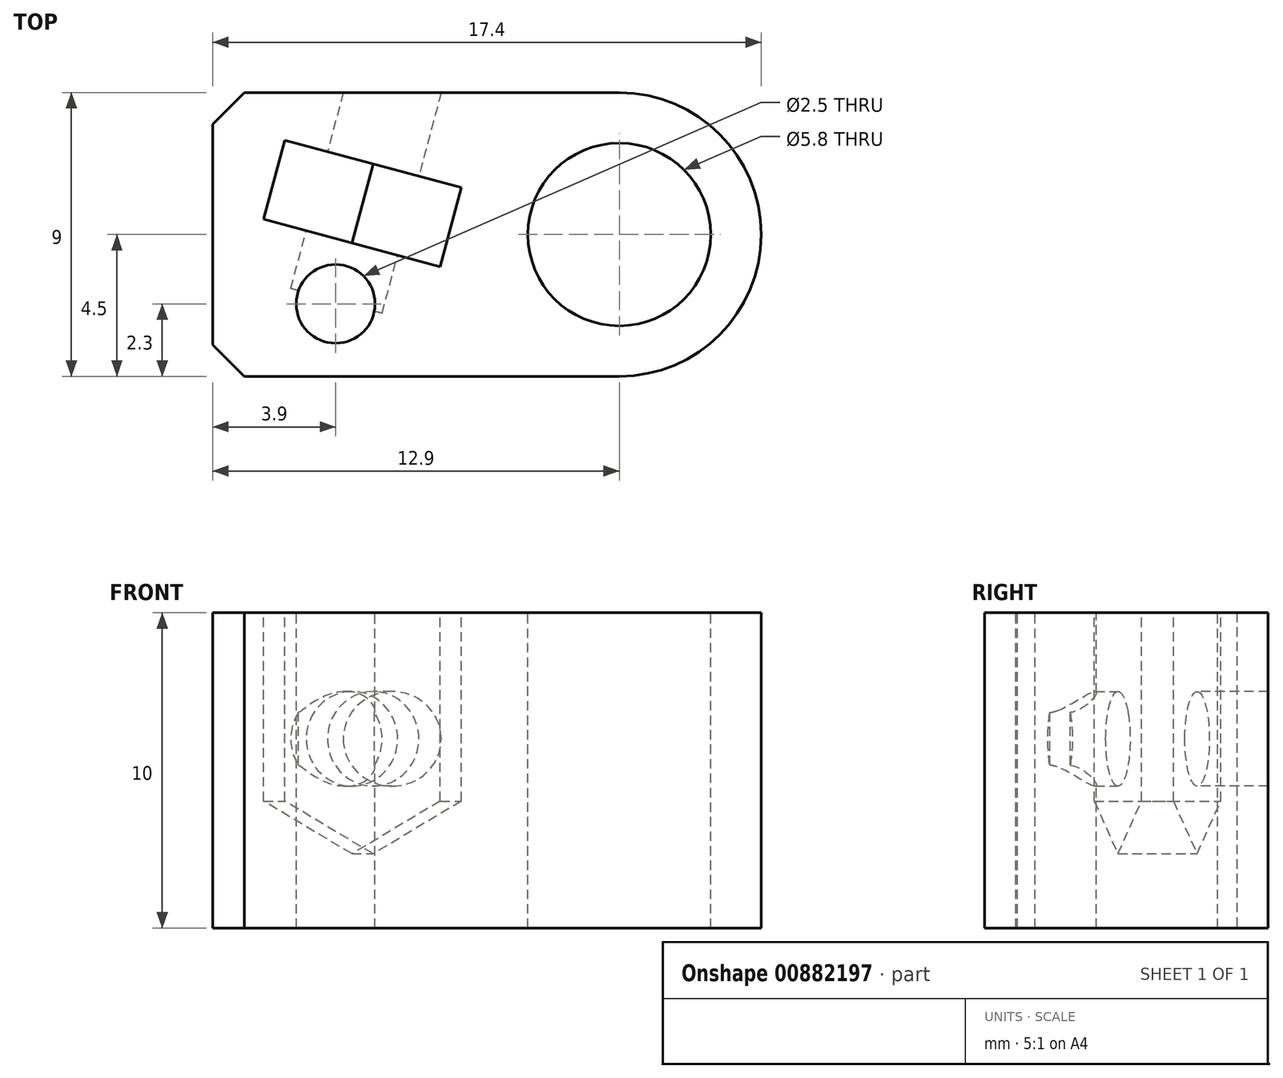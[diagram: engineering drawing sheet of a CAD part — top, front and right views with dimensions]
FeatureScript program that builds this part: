
annotation { "Feature Type Name" : "Feature", "Feature Type Description" : "" }
export const myFeature = defineFeature(function(context is Context, id is Id, definition is map)
    precondition{}
    {
        {
            var Q0;
            Q0=qCreatedBy(makeId("Top.planeOp"),FACE);
            var sketch = newSketch(context, id + "F0", { "sketchPlane" : qUnion([Q0])});
            skLineSegment(sketch, "E0.bottom", {"start": v(0, 0) * mm, "end": v(12.9, 0) * mm});
            skLineSegment(sketch, "E0.top", {"start": v(0, 9) * mm, "end": v(12.9, 9) * mm});
            skLineSegment(sketch, "E0.left", {"start": v(0, 0) * mm, "end": v(0, 9) * mm});
            skLineSegment(sketch, "E0.right", {"start": v(12.9, 0) * mm, "end": v(12.9, 9) * mm});
            skCircle(sketch, "E1", {"center": v(12.9, 4.5) * mm, "radius": 4.5 * mm});
            skCircle(sketch, "E2", {"center": v(12.9, 4.5) * mm, "radius": 2.9 * mm});
            skCircle(sketch, "E3", {"center": v(3.9, 2.3) * mm, "radius": 1.25 * mm});
            skSolve(sketch);
        }
        {
            var Q0;
            Q0=qSketchRegion(id+"F0",true);
            extrude(context, id + "F1", {"entities" : qUnion([Q0]), "oppositeDirection" : true, "depth" : 10 * mm, "offsetDistance" : 25 * mm});
        }
        {
            var Q0;
            Q0=makeQuery(id+"F1.opExtrude","CAP_FACE",FACE,{"disambiguationData":[OSD([sQuery(id+"F0.wireOp",EDGE,"E0.bottom"),sQuery(id+"F0.wireOp",EDGE,"E0.top"),sQuery(id+"F0.wireOp",EDGE,"E0.left"),sQuery(id+"F0.wireOp",EDGE,"E1"),sQuery(id+"F0.wireOp",EDGE,"E2"),sQuery(id+"F0.wireOp",EDGE,"E3")])],"isStart":true});
            var sketch = newSketch(context, id + "F2", { "sketchPlane" : qUnion([Q0])});
            skLineSegment(sketch, "E4.bottom", {"start": v(2.29, 7.5) * mm, "end": v(7.9, 6) * mm});
            skLineSegment(sketch, "E4.top", {"start": v(1.62, 4.98) * mm, "end": v(7.22, 3.48) * mm});
            skLineSegment(sketch, "E4.left", {"start": v(2.29, 7.5) * mm, "end": v(1.62, 4.98) * mm});
            skLineSegment(sketch, "E4.right", {"start": v(7.9, 6) * mm, "end": v(7.22, 3.48) * mm});
            skPoint(sketch, "E5", {"position": v(3.9, 2.3) * mm});
            skLineSegment(sketch, "E6", {"start": v(1.18, 2.3) * mm, "end": v(6.9, 2.3) * mm, "construction": true});
            skLineSegment(sketch, "E7", {"start": v(3.9, 2.3) * mm, "end": v(4.42, 4.23) * mm, "construction": true});
            skSolve(sketch);
        }
        {
            var Q0;
            Q0=makeQuery(id+"F2.imprint","IMPRINT",FACE,{"disambiguationData":[TD([[makeQuery(id+"F2.imprint","IMPRINT",EDGE,{"derivedFrom":sQuery(id+"F2.wireOp",EDGE,"E4.bottom")}),-1.0]])]});
            extrude(context, id + "F3", {"entities" : qUnion([Q0]), "operationType" : NewBodyOperationType.REMOVE, "oppositeDirection" : true, "depth" : 5 * mm, "offsetDistance" : 25 * mm});
        }
        {
            var Q0;
            Q0=makeQuery(id+"F3.boolean.opBoolean","COPY",FACE,{"derivedFrom":makeQuery(id+"F3.opExtrude","SWEPT_FACE",FACE,{"disambiguationData":[OSD([sQuery(id+"F2.wireOp",EDGE,"E4.bottom")])]})});
            var sketch = newSketch(context, id + "F4", { "sketchPlane" : qUnion([Q0])});
            skLineSegment(sketch, "E8.bottom", {"start": v(0.27, 0) * mm, "end": v(6.07, 0) * mm, "construction": true});
            skLineSegment(sketch, "E8.left", {"start": v(0.27, 0) * mm, "end": v(0.27, -5) * mm, "construction": true});
            skLineSegment(sketch, "E8.right", {"start": v(6.07, 0) * mm, "end": v(6.07, -5) * mm, "construction": true});
            skCircle(sketch, "E9.cCircle", {"center": v(3.17, -4.3) * mm, "radius": 2.9 * mm, "construction": true});
            skPoint(sketch, "E9.cCircle.centerSnap0", {"position": v(3.17, -5) * mm});
            skLineSegment(sketch, "E9.0", {"start": v(6.07, -2.63) * mm, "end": v(6.07, -5.97) * mm});
            skLineSegment(sketch, "E9.1", {"start": v(6.07, -5.97) * mm, "end": v(3.17, -7.65) * mm});
            skLineSegment(sketch, "E9.2", {"start": v(3.17, -7.65) * mm, "end": v(0.27, -5.97) * mm});
            skLineSegment(sketch, "E9.3", {"start": v(0.27, -5.97) * mm, "end": v(0.27, -2.63) * mm});
            skLineSegment(sketch, "E9.4", {"start": v(0.27, -2.63) * mm, "end": v(3.17, -0.95) * mm});
            skLineSegment(sketch, "E9.5", {"start": v(3.17, -0.95) * mm, "end": v(6.07, -2.63) * mm});
            skPoint(sketch, "E9.0.midPoint", {"position": v(6.07, -4.3) * mm});
            skSolve(sketch);
        }
        {
            var Q0;
            Q0=qSketchRegion(id+"F4",true);
            var Q1;
            Q1=makeQuery(id+"F3.boolean.opBoolean","COPY",VERTEX,{"derivedFrom":makeQuery(id+"F3.opExtrude","CAP_VERTEX",VERTEX,{"disambiguationData":[OSD([sQuery(id+"F2.wireOp",EDGE,"E4.top"),sQuery(id+"F2.wireOp",EDGE,"E4.right")])],"isStart":false})});
            extrude(context, id + "F5", {"entities" : qUnion([Q0]), "operationType" : NewBodyOperationType.REMOVE, "endBound" : BoundingType.UP_TO_VERTEX, "depth" : 25 * mm, "endBoundEntityVertex" : qUnion([Q1]), "offsetDistance" : 25 * mm});
        }
        {
            var Q0;
            Q0=makeQuery(id+"F5.boolean.opBoolean","MERGE",FACE,{"derivedFrom":[makeQuery(id+"F3.boolean.opBoolean","COPY",FACE,{"derivedFrom":makeQuery(id+"F3.opExtrude","SWEPT_FACE",FACE,{"disambiguationData":[OSD([sQuery(id+"F2.wireOp",EDGE,"E4.bottom")])]})}),makeQuery(id+"F5.opExtrude","CAP_FACE",FACE,{"disambiguationData":[OSD([sQuery(id+"F4.wireOp",EDGE,"E9.0"),sQuery(id+"F4.wireOp",EDGE,"E9.1"),sQuery(id+"F4.wireOp",EDGE,"E9.2"),sQuery(id+"F4.wireOp",EDGE,"E9.3"),sQuery(id+"F4.wireOp",EDGE,"E9.4"),sQuery(id+"F4.wireOp",EDGE,"E9.5")])],"isStart":true})]});
            var sketch = newSketch(context, id + "F6", { "sketchPlane" : qUnion([Q0])});
            skLineSegment(sketch, "E10.bottom", {"start": v(0.27, 0) * mm, "end": v(6.07, 0) * mm, "construction": true});
            skLineSegment(sketch, "E10.top", {"start": v(0.27, -5.97) * mm, "end": v(6.07, -5.97) * mm, "construction": true});
            skLineSegment(sketch, "E10.left", {"start": v(0.27, 0) * mm, "end": v(0.27, -5.97) * mm, "construction": true});
            skLineSegment(sketch, "E10.right", {"start": v(6.07, 0) * mm, "end": v(6.07, -5.97) * mm, "construction": true});
            skLineSegment(sketch, "E11", {"start": v(3.17, 0) * mm, "end": v(3.17, -5.97) * mm, "construction": true});
            skCircle(sketch, "E12", {"center": v(3.17, -4) * mm, "radius": 1.5 * mm});
            skSolve(sketch);
        }
        {
            var Q0;
            Q0=qSketchRegion(id+"F6",true);
            extrude(context, id + "F7", {"entities" : qUnion([Q0]), "operationType" : NewBodyOperationType.REMOVE, "oppositeDirection" : true, "depth" : 3 * mm, "offsetDistance" : 25 * mm});
        }
        {
            var Q0;
            Q0=qSketchRegion(id+"F6",true);
            extrude(context, id + "F8", {"entities" : qUnion([Q0]), "operationType" : NewBodyOperationType.REMOVE, "depth" : 4.5 * mm, "offsetDistance" : 25 * mm});
        }
        {
            var Q0;
            Q0=makeQuery(id+"F1.opExtrude","SWEPT_EDGE",EDGE,{"disambiguationData":[OSD([sQuery(id+"F0.wireOp",EDGE,"E0.bottom"),sQuery(id+"F0.wireOp",EDGE,"E0.left")])]});
            chamfer(context, id + "F9", {"entities" : qUnion([Q0]), "width" : 1 * mm, "tangentPropagation" : true});
        }
        {
            var Q0;
            Q0=makeQuery(id+"F1.opExtrude","SWEPT_EDGE",EDGE,{"disambiguationData":[OSD([sQuery(id+"F0.wireOp",EDGE,"E0.top"),sQuery(id+"F0.wireOp",EDGE,"E0.left")])]});
            chamfer(context, id + "F10", {"entities" : qUnion([Q0]), "width" : 1 * mm, "tangentPropagation" : true});
        }
    });
